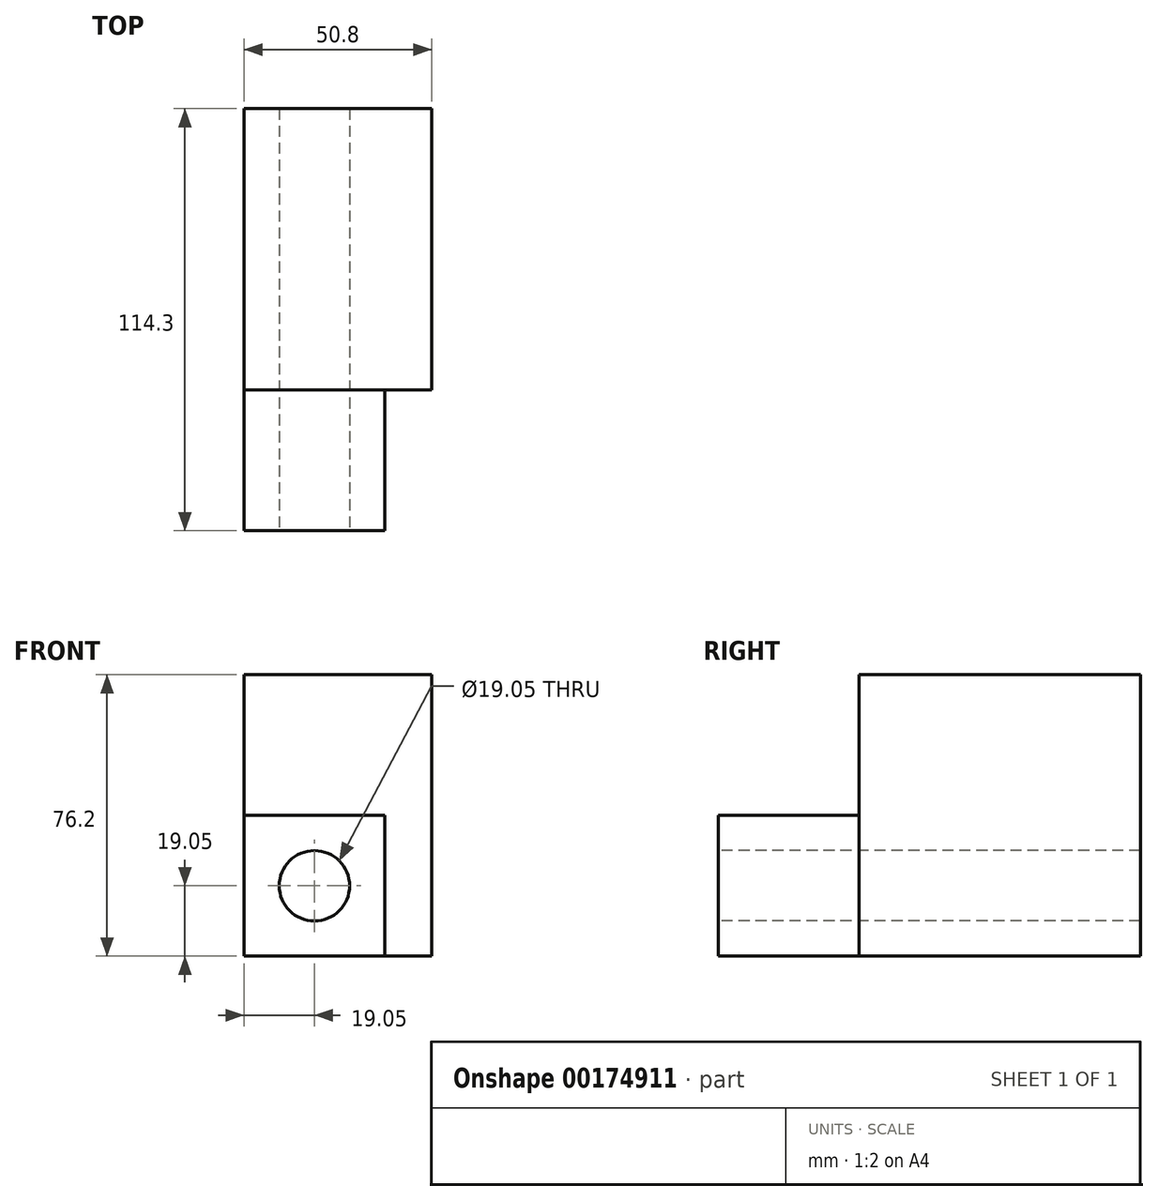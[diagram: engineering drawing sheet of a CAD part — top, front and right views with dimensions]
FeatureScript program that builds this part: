
annotation { "Feature Type Name" : "Feature", "Feature Type Description" : "" }
export const myFeature = defineFeature(function(context is Context, id is Id, definition is map)
    precondition{}
    {
        {
            var Q0;
            Q0=qCreatedBy(makeId("Front.planeOp"),FACE);
            var sketch = newSketch(context, id + "F0", { "sketchPlane" : qUnion([Q0])});
            skLineSegment(sketch, "E0.bottom", {"start": v(0, 0) * mm, "end": v(50.8, 0) * mm});
            skLineSegment(sketch, "E0.top", {"start": v(0, 76.2) * mm, "end": v(50.8, 76.2) * mm});
            skLineSegment(sketch, "E0.left", {"start": v(0, 0) * mm, "end": v(0, 76.2) * mm});
            skLineSegment(sketch, "E0.right", {"start": v(50.8, 0) * mm, "end": v(50.8, 76.2) * mm});
            skSolve(sketch);
        }
        {
            var Q0;
            Q0=makeQuery(id+"F0.imprint","IMPRINT",FACE,{"disambiguationData":[TD([[makeQuery(id+"F0.imprint","IMPRINT",EDGE,{"derivedFrom":sQuery(id+"F0.wireOp",EDGE,"E0.bottom")}),1.0]])]});
            extrude(context, id + "F1", {"entities" : qUnion([Q0]), "depth" : 76.2 * mm});
        }
        {
            var Q0;
            Q0=makeQuery(id+"F1.opExtrude","CAP_FACE",FACE,{"disambiguationData":[OSD([sQuery(id+"F0.wireOp",EDGE,"E0.bottom"),sQuery(id+"F0.wireOp",EDGE,"E0.top"),sQuery(id+"F0.wireOp",EDGE,"E0.left"),sQuery(id+"F0.wireOp",EDGE,"E0.right")])],"isStart":false});
            var sketch = newSketch(context, id + "F2", { "sketchPlane" : qUnion([Q0])});
            skLineSegment(sketch, "E1.bottom", {"start": v(0, 0) * mm, "end": v(38.1, 0) * mm});
            skLineSegment(sketch, "E1.top", {"start": v(0, 38.1) * mm, "end": v(38.1, 38.1) * mm});
            skLineSegment(sketch, "E1.left", {"start": v(0, 0) * mm, "end": v(0, 38.1) * mm});
            skLineSegment(sketch, "E1.right", {"start": v(38.1, 0) * mm, "end": v(38.1, 38.1) * mm});
            skSolve(sketch);
        }
        {
            var Q0;
            Q0 = qSketchRegion(id + "F2", true);
            extrude(context, id + "F3", {"entities" : qUnion([Q0]), "operationType" : NewBodyOperationType.ADD, "depth" : 38.1 * mm});
        }
        {
            var Q0;
            Q0=makeQuery(id+"F3.opExtrude","CAP_FACE",FACE,{"disambiguationData":[OSD([sQuery(id+"F2.wireOp",EDGE,"E1.bottom"),sQuery(id+"F2.wireOp",EDGE,"E1.top"),sQuery(id+"F2.wireOp",EDGE,"E1.left"),sQuery(id+"F2.wireOp",EDGE,"E1.right")])],"isStart":false});
            var sketch = newSketch(context, id + "F4", { "sketchPlane" : qUnion([Q0])});
            skCircle(sketch, "E2", {"center": v(19.05, 19.05) * mm, "radius": 9.53 * mm});
            skSolve(sketch);
        }
        {
            var Q0;
            Q0=makeQuery(id+"F4.imprint","IMPRINT",FACE,{"disambiguationData":[TD([[makeQuery(id+"F4.imprint","IMPRINT",EDGE,{"derivedFrom":sQuery(id+"F4.wireOp",EDGE,"E2")}),1.0]])]});
            extrude(context, id + "F5", {"entities" : qUnion([Q0]), "operationType" : NewBodyOperationType.REMOVE, "oppositeDirection" : true, "depth" : 114.3 * mm});
        }
    });
